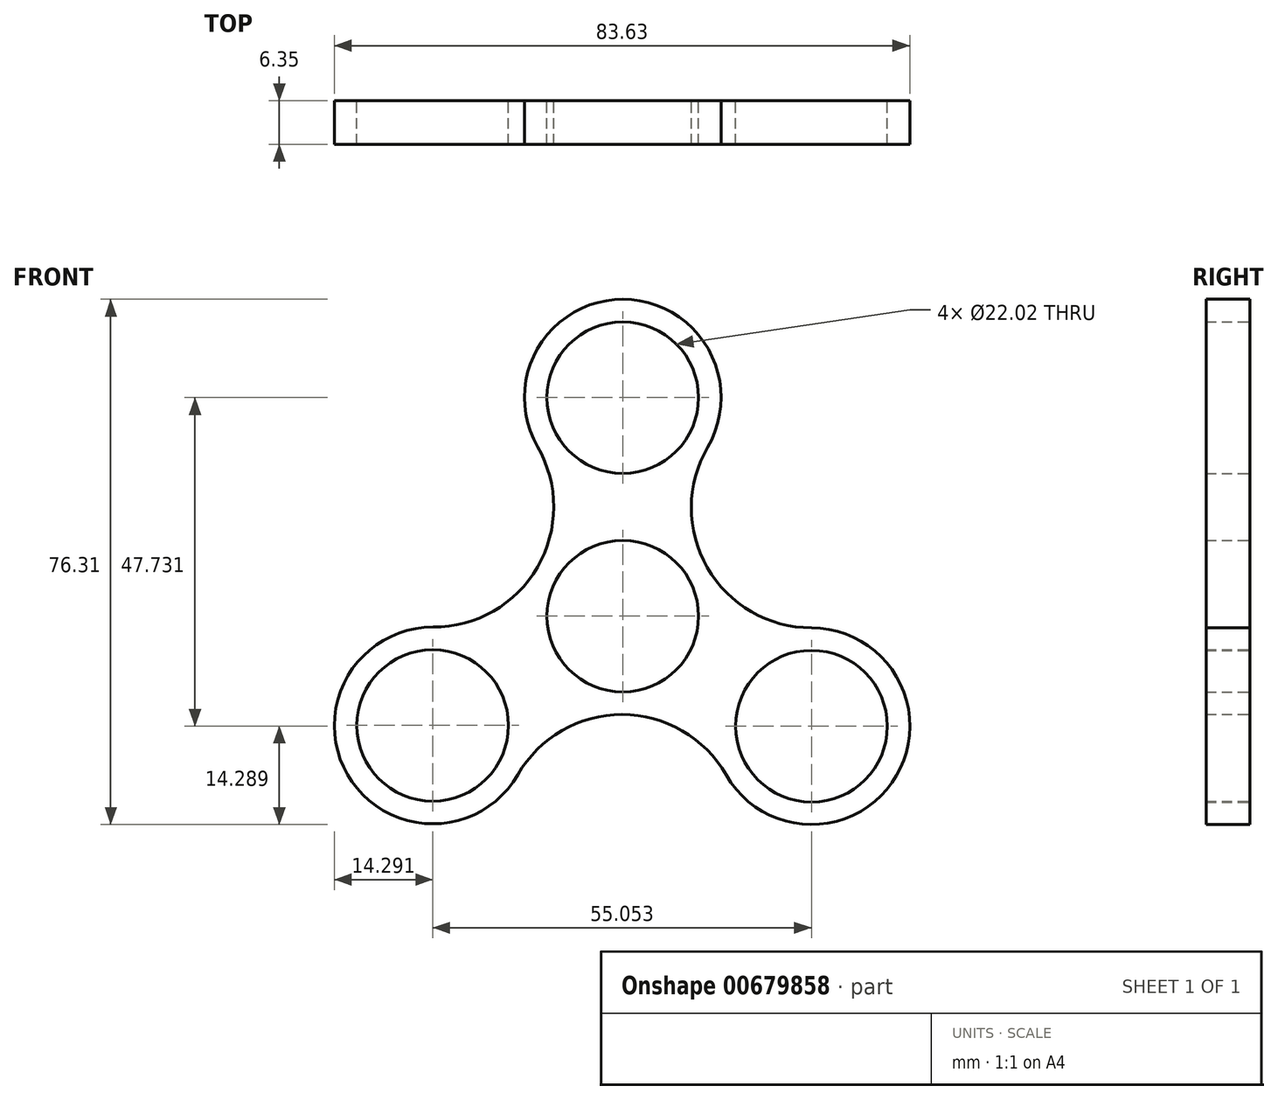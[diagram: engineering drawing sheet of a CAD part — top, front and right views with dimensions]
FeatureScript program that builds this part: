
annotation { "Feature Type Name" : "Feature", "Feature Type Description" : "" }
export const myFeature = defineFeature(function(context is Context, id is Id, definition is map)
    precondition{}
    {
        {
            var Q0;
            Q0=qCreatedBy(makeId("Front.planeOp"),FACE);
            var sketch = newSketch(context, id + "F0", { "sketchPlane" : qUnion([Q0])});
            skCircle(sketch, "E0", {"center": v(0, 0) * mm, "radius": 14.29 * mm});
            skCircle(sketch, "E1", {"center": v(0, 0) * mm, "radius": 11.01 * mm});
            skCircle(sketch, "E2", {"center": v(0, 31.75) * mm, "radius": 14.29 * mm});
            skCircle(sketch, "E3", {"center": v(0, 31.75) * mm, "radius": 11.01 * mm});
            skCircle(sketch, "E4.1.0", {"center": v(-27.62, -15.87) * mm, "radius": 11.01 * mm});
            skCircle(sketch, "E4.1.1", {"center": v(-27.62, -15.87) * mm, "radius": 14.29 * mm});
            skCircle(sketch, "E4.2.0", {"center": v(27.44, -15.98) * mm, "radius": 11.01 * mm});
            skCircle(sketch, "E4.2.1", {"center": v(27.44, -15.98) * mm, "radius": 14.29 * mm});
            skPoint(sketch, "E4.center", {"position": v(-0.06, -0.04) * mm});
            skCircle(sketch, "E5", {"center": v(-27.5, 15.88) * mm, "radius": 17.46 * mm});
            skCircle(sketch, "E6.1.0", {"center": v(-0.12, -31.75) * mm, "radius": 17.46 * mm});
            skCircle(sketch, "E6.2.0", {"center": v(27.44, 15.77) * mm, "radius": 17.46 * mm});
            skSolve(sketch);
        }
        {
            var Q0;
            Q0=makeQuery(id+"F0.imprint","IMPRINT",FACE,{"disambiguationData":[TD([[makeQuery(id+"F0.imprint","IMPRINT",EDGE,{"derivedFrom":sQuery(id+"F0.wireOp",EDGE,"E3")}),-1.0]])]});
            var Q1;
            {var subQ0=sQuery(id+"F0.wireOp",EDGE,"E6.2.0");var subQ1=sQuery(id+"F0.wireOp",EDGE,"E0");var subQ2=makeQuery(id+"F0.imprint","INTERSECT",VERTEX,{"disambiguationData":[OD(0.0)],"derivedFrom":[subQ1,subQ0]});Q1=makeQuery(id+"F0.imprint","IMPRINT",FACE,{"disambiguationData":[TD([[makeQuery(id+"F0.imprint","IMPRINT",EDGE,{"disambiguationData":[TD([[subQ2,-1.0]])],"derivedFrom":subQ1}),-1.0]])]});}
            var Q2;
            Q2=makeQuery(id+"F0.imprint","IMPRINT",FACE,{"disambiguationData":[TD([[makeQuery(id+"F0.imprint","IMPRINT",EDGE,{"derivedFrom":sQuery(id+"F0.wireOp",EDGE,"E1")}),-1.0]])]});
            var Q3;
            {var subQ0=sQuery(id+"F0.wireOp",EDGE,"E5");var subQ1=sQuery(id+"F0.wireOp",EDGE,"E0");var subQ2=makeQuery(id+"F0.imprint","INTERSECT",VERTEX,{"derivedFrom":[subQ1,subQ0]});Q3=makeQuery(id+"F0.imprint","IMPRINT",FACE,{"disambiguationData":[TD([[makeQuery(id+"F0.imprint","IMPRINT",EDGE,{"disambiguationData":[TD([[subQ2,-1.0]])],"derivedFrom":subQ1}),-1.0]])]});}
            var Q4;
            Q4=makeQuery(id+"F0.imprint","IMPRINT",FACE,{"disambiguationData":[TD([[makeQuery(id+"F0.imprint","IMPRINT",EDGE,{"derivedFrom":sQuery(id+"F0.wireOp",EDGE,"E4.1.0")}),-1.0]])]});
            var Q5;
            {var subQ0=sQuery(id+"F0.wireOp",EDGE,"E6.2.0");var subQ1=sQuery(id+"F0.wireOp",EDGE,"E0");var subQ2=makeQuery(id+"F0.imprint","INTERSECT",VERTEX,{"disambiguationData":[OD(1.0)],"derivedFrom":[subQ1,subQ0]});Q5=makeQuery(id+"F0.imprint","IMPRINT",FACE,{"disambiguationData":[TD([[makeQuery(id+"F0.imprint","IMPRINT",EDGE,{"disambiguationData":[TD([[subQ2,1.0]])],"derivedFrom":subQ1}),-1.0]])]});}
            var Q6;
            Q6=makeQuery(id+"F0.imprint","IMPRINT",FACE,{"disambiguationData":[TD([[makeQuery(id+"F0.imprint","IMPRINT",EDGE,{"derivedFrom":sQuery(id+"F0.wireOp",EDGE,"E4.2.0")}),-1.0]])]});
            extrude(context, id + "F1", {"entities" : qUnion([Q0, Q1, Q2, Q3, Q4, Q5, Q6]), "depth" : 6.35 * mm, "offsetDistance" : 25.4 * mm});
        }
    });
